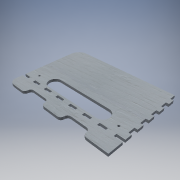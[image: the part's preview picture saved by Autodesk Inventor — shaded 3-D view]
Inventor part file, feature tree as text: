
AUTODESK INVENTOR PART (.ipt)
format: ipt  version: 2018.3 (Build 223284000, 284)  size: 221,184 bytes
history: native  units: mm
features: reference x12, other x4, extrude x3, sketch x3, fillet x2
ambient origin geometry x8: Origin, YZ Plane, XZ Plane, XY Plane, X Axis, Y Axis, Z Axis, Center Point
bodies: Solido1 (feature_tree)
feature tree (24):
  extrude  "Estrusione1"  Depth=80.0mm
  extrude  "Estrusione2"  Depth=4.0mm TaperAngle=0.0deg
  fillet  "Raccordo1"  Radius=4.0mm
  fillet  "Raccordo2"  Radius=15.0mm
  extrude  "Estrusione3"  Depth=10.0mm
  sketch  "Schizzo1"
  reference  "Riferimento14"
  reference  "Riferimento15"
  reference  "Riferimento16"
  reference  "Riferimento17"
  reference  "Riferimento18"
  reference  "Riferimento19"
  reference  "Riferimento20"
  reference  "Riferimento21"
  sketch  "Schizzo2"
  sketch  "Schizzo3"
  reference  "Riferimento22"
  reference  "Riferimento23"
  reference  "Riferimento24"
  reference  "Riferimento25"
  other  "<userpath>\Desktop\Scorbot Hardware\Case Board\caseHw.iam"
  other  "caseHw.iam"
  other  "tavolaBase:1"
  other  "Dietro:1"
